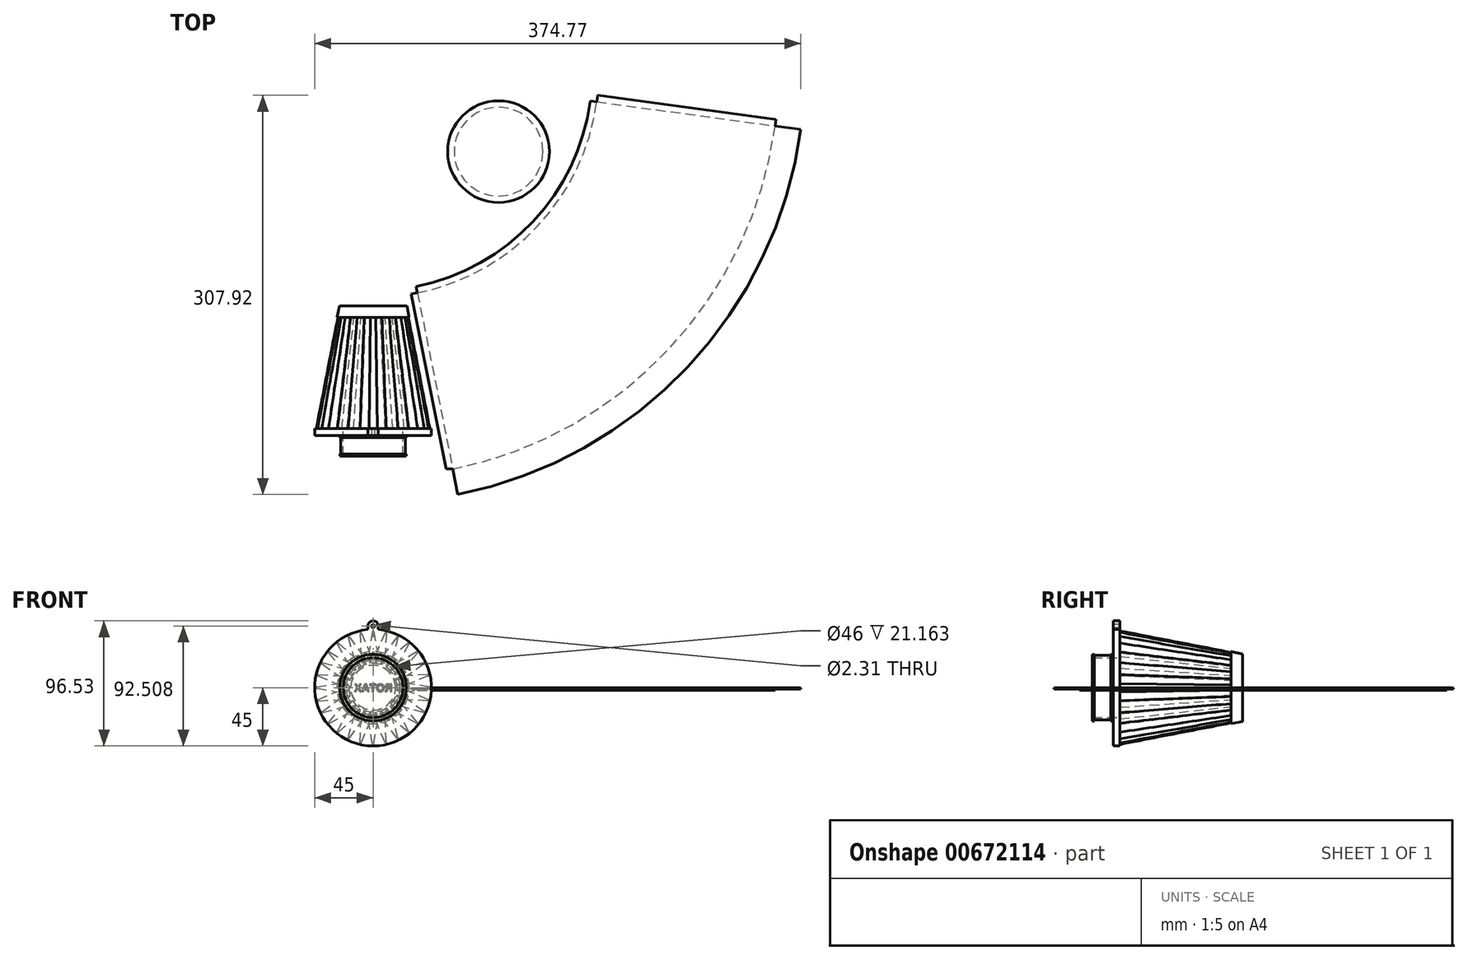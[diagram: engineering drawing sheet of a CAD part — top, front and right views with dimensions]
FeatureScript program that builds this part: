
annotation { "Feature Type Name" : "Feature", "Feature Type Description" : "" }
export const myFeature = defineFeature(function(context is Context, id is Id, definition is map)
    precondition{}
    {
        {
            var Q0;
            Q0=qCreatedBy(makeId("Top.planeOp"),FACE);
            var sketch = newSketch(context, id + "F0", { "sketchPlane" : qUnion([Q0])});
            skLineSegment(sketch, "E0", {"start": v(0, 51.66) * mm, "end": v(0, -26.1) * mm, "construction": true});
            skLineSegment(sketch, "E1.bottom", {"start": v(23, 0) * mm, "end": v(25.69, 0) * mm});
            skLineSegment(sketch, "E1.top", {"start": v(23, -16) * mm, "end": v(25.69, -16) * mm});
            skLineSegment(sketch, "E1.left", {"start": v(23, 5.16) * mm, "end": v(23, -16) * mm});
            skLineSegment(sketch, "E1.right", {"start": v(25.69, 0) * mm, "end": v(25.69, -1.62) * mm});
            skLineSegment(sketch, "E2.bottom", {"start": v(23, 0) * mm, "end": v(45, 0) * mm});
            skLineSegment(sketch, "E2.top", {"start": v(23, 5.16) * mm, "end": v(45, 5.16) * mm});
            skLineSegment(sketch, "E2.left", {"start": v(0, 0) * mm, "end": v(0, 5.16) * mm});
            skLineSegment(sketch, "E2.right", {"start": v(45, 0) * mm, "end": v(45, 5.16) * mm});
            skLineSegment(sketch, "E3.bottom", {"start": v(0, 100) * mm, "end": v(26, 100) * mm});
            skLineSegment(sketch, "E3.top", {"start": v(0, 90.86) * mm, "end": v(27.83, 90.86) * mm});
            skLineSegment(sketch, "E3.left", {"start": v(0, 100) * mm, "end": v(0, 90.86) * mm});
            skLineSegment(sketch, "E3.right", {"start": v(26, 100) * mm, "end": v(27.83, 90.86) * mm});
            skLineSegment(sketch, "E4", {"start": v(27.83, 90.86) * mm, "end": v(45, 5.16) * mm, "construction": true});
            skLineSegment(sketch, "E5.bottom", {"start": v(23, 5.16) * mm, "end": v(0, 5.16) * mm});
            skLineSegment(sketch, "E5.top", {"start": v(23, 0) * mm, "end": v(0, 0) * mm});
            skLineSegment(sketch, "E5.left", {"start": v(23, 5.16) * mm, "end": v(23, 0) * mm});
            skLineSegment(sketch, "E5.right", {"start": v(0, 5.16) * mm, "end": v(0, 0) * mm});
            skLineSegment(sketch, "E6.bottom", {"start": v(25.69, -14.38) * mm, "end": v(24.93, -14.38) * mm});
            skLineSegment(sketch, "E6.top", {"start": v(25.69, -1.62) * mm, "end": v(24.93, -1.62) * mm});
            skLineSegment(sketch, "E6.right", {"start": v(24.93, -14.38) * mm, "end": v(24.93, -1.62) * mm});
            skLineSegment(sketch, "E7.trimOffspring", {"start": v(25.69, -14.38) * mm, "end": v(25.69, -16) * mm});
            skSolve(sketch);
        }
        {
            var Q0;
            Q0=makeQuery(id+"F0.imprint","IMPRINT",FACE,{"disambiguationData":[TD([[makeQuery(id+"F0.imprint","IMPRINT",EDGE,{"derivedFrom":sQuery(id+"F0.wireOp",EDGE,"E3.bottom")}),-1.0]])]});
            var Q1;
            Q1=makeQuery(id+"F0.imprint","IMPRINT",FACE,{"disambiguationData":[TD([[makeQuery(id+"F0.imprint","IMPRINT",EDGE,{"derivedFrom":sQuery(id+"F0.wireOp",EDGE,"E1.top")}),1.0]])]});
            var Q2;
            Q2=makeQuery(id+"F0.imprint","IMPRINT",FACE,{"disambiguationData":[TD([[makeQuery(id+"F0.imprint","IMPRINT",EDGE,{"derivedFrom":sQuery(id+"F0.wireOp",EDGE,"E5.bottom")}),1.0]])]});
            var Q3;
            Q3=makeQuery(id+"F0.imprint","IMPRINT",FACE,{"disambiguationData":[TD([[makeQuery(id+"F0.imprint","IMPRINT",EDGE,{"derivedFrom":sQuery(id+"F0.wireOp",EDGE,"E2.top")}),-1.0]])]});
            var Q4;
            Q4=sQuery(id+"F0.wireOp",EDGE,"E0");
            revolve(context, id + "F1", {"entities" : qUnion([Q0, Q1, Q2, Q3]), "axis" : qUnion([Q4]), "revolveType" : RevolveType.FULL});
        }
        {
            var Q0;
            Q0=makeQuery(id+"F1.opRevolve","SWEPT_FACE",FACE,{"disambiguationData":[OSD([sQuery(id+"F0.wireOp",EDGE,"E2.top")])]});
            var sketch = newSketch(context, id + "F2", { "sketchPlane" : qUnion([Q0])});
            skLineSegment(sketch, "E8", {"start": v(0.5, 43.39) * mm, "end": v(3.18, 28.2) * mm});
            skLineSegment(sketch, "E9", {"start": v(0, 17.46) * mm, "end": v(0, -16.12) * mm, "construction": true});
            skLineSegment(sketch, "E10.MirrorCS", {"start": v(-0.5, 43.39) * mm, "end": v(-3.18, 28.2) * mm});
            skPoint(sketch, "E11.visualSharp", {"position": v(0, 46.17) * mm});
            skArc(sketch, "E11.filletArc", {"start": v(0.5, 43.39) * mm, "mid": v(0, 43.8) * mm, "end": v(-0.5, 43.39) * mm});
            skLineSegment(sketch, "E12.1.0", {"start": v(-10.13, 42.2) * mm, "end": v(-9.37, 26.79) * mm});
            skArc(sketch, "E12.1.1", {"start": v(-9.17, 42.41) * mm, "mid": v(-9.75, 42.7) * mm, "end": v(-10.13, 42.2) * mm});
            skLineSegment(sketch, "E12.1.2", {"start": v(-9.17, 42.41) * mm, "end": v(-3.18, 28.2) * mm});
            skLineSegment(sketch, "E12.2.0", {"start": v(-19.27, 38.88) * mm, "end": v(-15.1, 24.03) * mm});
            skArc(sketch, "E12.2.1", {"start": v(-18.38, 39.3) * mm, "mid": v(-19, 39.46) * mm, "end": v(-19.27, 38.88) * mm});
            skLineSegment(sketch, "E12.2.2", {"start": v(-18.38, 39.3) * mm, "end": v(-9.37, 26.79) * mm});
            skLineSegment(sketch, "E12.3.0", {"start": v(-27.44, 33.62) * mm, "end": v(-20.07, 20.07) * mm});
            skArc(sketch, "E12.3.1", {"start": v(-26.67, 34.23) * mm, "mid": v(-27.31, 34.25) * mm, "end": v(-27.44, 33.62) * mm});
            skLineSegment(sketch, "E12.3.2", {"start": v(-26.67, 34.23) * mm, "end": v(-15.1, 24.03) * mm});
            skLineSegment(sketch, "E12.4.0", {"start": v(-34.23, 26.67) * mm, "end": v(-24.03, 15.1) * mm});
            skArc(sketch, "E12.4.1", {"start": v(-33.62, 27.44) * mm, "mid": v(-34.25, 27.31) * mm, "end": v(-34.23, 26.67) * mm});
            skLineSegment(sketch, "E12.4.2", {"start": v(-33.62, 27.44) * mm, "end": v(-20.07, 20.07) * mm});
            skLineSegment(sketch, "E12.5.0", {"start": v(-39.3, 18.38) * mm, "end": v(-26.79, 9.37) * mm});
            skArc(sketch, "E12.5.1", {"start": v(-38.88, 19.27) * mm, "mid": v(-39.46, 19) * mm, "end": v(-39.3, 18.38) * mm});
            skLineSegment(sketch, "E12.5.2", {"start": v(-38.88, 19.27) * mm, "end": v(-24.03, 15.1) * mm});
            skLineSegment(sketch, "E12.6.0", {"start": v(-42.41, 9.17) * mm, "end": v(-28.2, 3.18) * mm});
            skArc(sketch, "E12.6.1", {"start": v(-42.2, 10.13) * mm, "mid": v(-42.7, 9.75) * mm, "end": v(-42.41, 9.17) * mm});
            skLineSegment(sketch, "E12.6.2", {"start": v(-42.2, 10.13) * mm, "end": v(-26.79, 9.37) * mm});
            skLineSegment(sketch, "E12.7.0", {"start": v(-43.39, -0.5) * mm, "end": v(-28.2, -3.18) * mm});
            skArc(sketch, "E12.7.1", {"start": v(-43.39, 0.5) * mm, "mid": v(-43.8, 0) * mm, "end": v(-43.39, -0.5) * mm});
            skLineSegment(sketch, "E12.7.2", {"start": v(-43.39, 0.5) * mm, "end": v(-28.2, 3.18) * mm});
            skLineSegment(sketch, "E12.8.0", {"start": v(-42.2, -10.13) * mm, "end": v(-26.79, -9.37) * mm});
            skArc(sketch, "E12.8.1", {"start": v(-42.41, -9.17) * mm, "mid": v(-42.7, -9.75) * mm, "end": v(-42.2, -10.13) * mm});
            skLineSegment(sketch, "E12.8.2", {"start": v(-42.41, -9.17) * mm, "end": v(-28.2, -3.18) * mm});
            skLineSegment(sketch, "E12.9.0", {"start": v(-38.88, -19.27) * mm, "end": v(-24.03, -15.1) * mm});
            skArc(sketch, "E12.9.1", {"start": v(-39.3, -18.38) * mm, "mid": v(-39.46, -19) * mm, "end": v(-38.88, -19.27) * mm});
            skLineSegment(sketch, "E12.9.2", {"start": v(-39.3, -18.38) * mm, "end": v(-26.79, -9.37) * mm});
            skLineSegment(sketch, "E12.10.0", {"start": v(-33.62, -27.44) * mm, "end": v(-20.07, -20.07) * mm});
            skArc(sketch, "E12.10.1", {"start": v(-34.23, -26.67) * mm, "mid": v(-34.25, -27.31) * mm, "end": v(-33.62, -27.44) * mm});
            skLineSegment(sketch, "E12.10.2", {"start": v(-34.23, -26.67) * mm, "end": v(-24.03, -15.1) * mm});
            skLineSegment(sketch, "E12.11.0", {"start": v(-26.67, -34.23) * mm, "end": v(-15.1, -24.03) * mm});
            skArc(sketch, "E12.11.1", {"start": v(-27.44, -33.62) * mm, "mid": v(-27.31, -34.25) * mm, "end": v(-26.67, -34.23) * mm});
            skLineSegment(sketch, "E12.11.2", {"start": v(-27.44, -33.62) * mm, "end": v(-20.07, -20.07) * mm});
            skLineSegment(sketch, "E12.12.0", {"start": v(-18.38, -39.3) * mm, "end": v(-9.37, -26.79) * mm});
            skArc(sketch, "E12.12.1", {"start": v(-19.27, -38.88) * mm, "mid": v(-19, -39.46) * mm, "end": v(-18.38, -39.3) * mm});
            skLineSegment(sketch, "E12.12.2", {"start": v(-19.27, -38.88) * mm, "end": v(-15.1, -24.03) * mm});
            skLineSegment(sketch, "E12.13.0", {"start": v(-9.17, -42.41) * mm, "end": v(-3.18, -28.2) * mm});
            skArc(sketch, "E12.13.1", {"start": v(-10.13, -42.2) * mm, "mid": v(-9.75, -42.7) * mm, "end": v(-9.17, -42.41) * mm});
            skLineSegment(sketch, "E12.13.2", {"start": v(-10.13, -42.2) * mm, "end": v(-9.37, -26.79) * mm});
            skLineSegment(sketch, "E12.14.0", {"start": v(0.5, -43.39) * mm, "end": v(3.18, -28.2) * mm});
            skArc(sketch, "E12.14.1", {"start": v(-0.5, -43.39) * mm, "mid": v(0, -43.8) * mm, "end": v(0.5, -43.39) * mm});
            skLineSegment(sketch, "E12.14.2", {"start": v(-0.5, -43.39) * mm, "end": v(-3.18, -28.2) * mm});
            skLineSegment(sketch, "E12.15.0", {"start": v(10.13, -42.2) * mm, "end": v(9.37, -26.79) * mm});
            skArc(sketch, "E12.15.1", {"start": v(9.17, -42.41) * mm, "mid": v(9.75, -42.7) * mm, "end": v(10.13, -42.2) * mm});
            skLineSegment(sketch, "E12.15.2", {"start": v(9.17, -42.41) * mm, "end": v(3.18, -28.2) * mm});
            skLineSegment(sketch, "E12.16.0", {"start": v(19.27, -38.88) * mm, "end": v(15.1, -24.03) * mm});
            skArc(sketch, "E12.16.1", {"start": v(18.38, -39.3) * mm, "mid": v(19, -39.46) * mm, "end": v(19.27, -38.88) * mm});
            skLineSegment(sketch, "E12.16.2", {"start": v(18.38, -39.3) * mm, "end": v(9.37, -26.79) * mm});
            skLineSegment(sketch, "E12.17.0", {"start": v(27.44, -33.62) * mm, "end": v(20.07, -20.07) * mm});
            skArc(sketch, "E12.17.1", {"start": v(26.67, -34.23) * mm, "mid": v(27.31, -34.25) * mm, "end": v(27.44, -33.62) * mm});
            skLineSegment(sketch, "E12.17.2", {"start": v(26.67, -34.23) * mm, "end": v(15.1, -24.03) * mm});
            skLineSegment(sketch, "E12.18.0", {"start": v(34.23, -26.67) * mm, "end": v(24.03, -15.1) * mm});
            skArc(sketch, "E12.18.1", {"start": v(33.62, -27.44) * mm, "mid": v(34.25, -27.31) * mm, "end": v(34.23, -26.67) * mm});
            skLineSegment(sketch, "E12.18.2", {"start": v(33.62, -27.44) * mm, "end": v(20.07, -20.07) * mm});
            skLineSegment(sketch, "E12.19.0", {"start": v(39.3, -18.38) * mm, "end": v(26.79, -9.37) * mm});
            skArc(sketch, "E12.19.1", {"start": v(38.88, -19.27) * mm, "mid": v(39.46, -19) * mm, "end": v(39.3, -18.38) * mm});
            skLineSegment(sketch, "E12.19.2", {"start": v(38.88, -19.27) * mm, "end": v(24.03, -15.1) * mm});
            skLineSegment(sketch, "E12.20.0", {"start": v(42.41, -9.17) * mm, "end": v(28.2, -3.18) * mm});
            skArc(sketch, "E12.20.1", {"start": v(42.2, -10.13) * mm, "mid": v(42.7, -9.75) * mm, "end": v(42.41, -9.17) * mm});
            skLineSegment(sketch, "E12.20.2", {"start": v(42.2, -10.13) * mm, "end": v(26.79, -9.37) * mm});
            skLineSegment(sketch, "E12.21.0", {"start": v(43.39, 0.5) * mm, "end": v(28.2, 3.18) * mm});
            skArc(sketch, "E12.21.1", {"start": v(43.39, -0.5) * mm, "mid": v(43.8, 0) * mm, "end": v(43.39, 0.5) * mm});
            skLineSegment(sketch, "E12.21.2", {"start": v(43.39, -0.5) * mm, "end": v(28.2, -3.18) * mm});
            skLineSegment(sketch, "E12.22.0", {"start": v(42.2, 10.13) * mm, "end": v(26.79, 9.37) * mm});
            skArc(sketch, "E12.22.1", {"start": v(42.41, 9.17) * mm, "mid": v(42.7, 9.75) * mm, "end": v(42.2, 10.13) * mm});
            skLineSegment(sketch, "E12.22.2", {"start": v(42.41, 9.17) * mm, "end": v(28.2, 3.18) * mm});
            skLineSegment(sketch, "E12.23.0", {"start": v(38.88, 19.27) * mm, "end": v(24.03, 15.1) * mm});
            skArc(sketch, "E12.23.1", {"start": v(39.3, 18.38) * mm, "mid": v(39.46, 19) * mm, "end": v(38.88, 19.27) * mm});
            skLineSegment(sketch, "E12.23.2", {"start": v(39.3, 18.38) * mm, "end": v(26.79, 9.37) * mm});
            skPoint(sketch, "E12.center", {"position": v(0, 0) * mm});
            skLineSegment(sketch, "E13.2.24.0", {"start": v(33.62, 27.44) * mm, "end": v(20.07, 20.07) * mm});
            skArc(sketch, "E13.3.24.0", {"start": v(34.23, 26.67) * mm, "mid": v(34.25, 27.31) * mm, "end": v(33.62, 27.44) * mm});
            skLineSegment(sketch, "E13.7.24.0", {"start": v(34.23, 26.67) * mm, "end": v(24.03, 15.1) * mm});
            skLineSegment(sketch, "E13.2.25.0", {"start": v(26.67, 34.23) * mm, "end": v(15.1, 24.03) * mm});
            skArc(sketch, "E13.3.25.0", {"start": v(27.44, 33.62) * mm, "mid": v(27.31, 34.25) * mm, "end": v(26.67, 34.23) * mm});
            skLineSegment(sketch, "E13.7.25.0", {"start": v(27.44, 33.62) * mm, "end": v(20.07, 20.07) * mm});
            skLineSegment(sketch, "E13.2.26.0", {"start": v(18.38, 39.3) * mm, "end": v(9.37, 26.79) * mm});
            skArc(sketch, "E13.3.26.0", {"start": v(19.27, 38.88) * mm, "mid": v(19, 39.46) * mm, "end": v(18.38, 39.3) * mm});
            skLineSegment(sketch, "E13.7.26.0", {"start": v(19.27, 38.88) * mm, "end": v(15.1, 24.03) * mm});
            skLineSegment(sketch, "E13.2.27.0", {"start": v(9.17, 42.41) * mm, "end": v(3.18, 28.2) * mm});
            skArc(sketch, "E13.3.27.0", {"start": v(10.13, 42.2) * mm, "mid": v(9.75, 42.7) * mm, "end": v(9.17, 42.41) * mm});
            skLineSegment(sketch, "E13.7.27.0", {"start": v(10.13, 42.2) * mm, "end": v(9.37, 26.79) * mm});
            skSolve(sketch);
        }
        {
            var Q0;
            Q0=makeQuery(id+"F1.opRevolve","SWEPT_FACE",FACE,{"disambiguationData":[OSD([sQuery(id+"F0.wireOp",EDGE,"E3.top")])]});
            var sketch = newSketch(context, id + "F3", { "sketchPlane" : qUnion([Q0])});
            skLineSegment(sketch, "E14", {"start": v(0, 0) * mm, "end": v(0, 35.69) * mm, "construction": true});
            skLineSegment(sketch, "E15", {"start": v(1, 26.37) * mm, "end": v(1.96, 17.37) * mm});
            skLineSegment(sketch, "E16.MirrorCS", {"start": v(-1, 26.37) * mm, "end": v(-1.96, 17.37) * mm});
            skPoint(sketch, "E17.visualSharp", {"position": v(0, 35.69) * mm});
            skArc(sketch, "E17.filletArc", {"start": v(1, 26.37) * mm, "mid": v(0, 27.27) * mm, "end": v(-1, 26.37) * mm});
            skLineSegment(sketch, "E18.1.0", {"start": v(-6.84, 25.5) * mm, "end": v(-5.77, 16.5) * mm});
            skArc(sketch, "E18.1.1", {"start": v(-4.9, 25.93) * mm, "mid": v(-6.07, 26.58) * mm, "end": v(-6.84, 25.5) * mm});
            skLineSegment(sketch, "E18.1.2", {"start": v(-4.9, 25.93) * mm, "end": v(-1.96, 17.37) * mm});
            skLineSegment(sketch, "E18.2.0", {"start": v(-12.33, 23.33) * mm, "end": v(-9.3, 14.8) * mm});
            skArc(sketch, "E18.2.1", {"start": v(-10.54, 24.2) * mm, "mid": v(-11.83, 24.57) * mm, "end": v(-12.33, 23.33) * mm});
            skLineSegment(sketch, "E18.2.2", {"start": v(-10.54, 24.2) * mm, "end": v(-5.77, 16.5) * mm});
            skLineSegment(sketch, "E18.3.0", {"start": v(-17.21, 20) * mm, "end": v(-12.35, 12.36) * mm});
            skArc(sketch, "E18.3.1", {"start": v(-15.66, 21.24) * mm, "mid": v(-17, 21.32) * mm, "end": v(-17.21, 20) * mm});
            skLineSegment(sketch, "E18.3.2", {"start": v(-15.66, 21.24) * mm, "end": v(-9.3, 14.8) * mm});
            skLineSegment(sketch, "E18.4.0", {"start": v(-21.23, 15.67) * mm, "end": v(-14.79, 9.3) * mm});
            skArc(sketch, "E18.4.1", {"start": v(-20, 17.22) * mm, "mid": v(-21.31, 17) * mm, "end": v(-21.23, 15.67) * mm});
            skLineSegment(sketch, "E18.4.2", {"start": v(-20, 17.22) * mm, "end": v(-12.35, 12.36) * mm});
            skLineSegment(sketch, "E18.5.0", {"start": v(-24.18, 10.55) * mm, "end": v(-16.49, 5.78) * mm});
            skArc(sketch, "E18.5.1", {"start": v(-23.32, 12.34) * mm, "mid": v(-24.56, 11.84) * mm, "end": v(-24.18, 10.55) * mm});
            skLineSegment(sketch, "E18.5.2", {"start": v(-23.32, 12.34) * mm, "end": v(-14.79, 9.3) * mm});
            skLineSegment(sketch, "E18.6.0", {"start": v(-25.92, 4.9) * mm, "end": v(-17.36, 1.96) * mm});
            skArc(sketch, "E18.6.1", {"start": v(-25.48, 6.84) * mm, "mid": v(-26.57, 6.07) * mm, "end": v(-25.92, 4.9) * mm});
            skLineSegment(sketch, "E18.6.2", {"start": v(-25.48, 6.84) * mm, "end": v(-16.49, 5.78) * mm});
            skLineSegment(sketch, "E18.7.0", {"start": v(-26.36, -0.99) * mm, "end": v(-17.36, -1.95) * mm});
            skArc(sketch, "E18.7.1", {"start": v(-26.36, 1) * mm, "mid": v(-27.26, 0) * mm, "end": v(-26.36, -0.99) * mm});
            skLineSegment(sketch, "E18.7.2", {"start": v(-26.36, 1) * mm, "end": v(-17.36, 1.96) * mm});
            skLineSegment(sketch, "E18.8.0", {"start": v(-25.48, -6.83) * mm, "end": v(-16.49, -5.76) * mm});
            skArc(sketch, "E18.8.1", {"start": v(-25.92, -4.89) * mm, "mid": v(-26.57, -6.06) * mm, "end": v(-25.48, -6.83) * mm});
            skLineSegment(sketch, "E18.8.2", {"start": v(-25.92, -4.89) * mm, "end": v(-17.36, -1.95) * mm});
            skLineSegment(sketch, "E18.9.0", {"start": v(-23.32, -12.33) * mm, "end": v(-14.79, -9.28) * mm});
            skArc(sketch, "E18.9.1", {"start": v(-24.18, -10.53) * mm, "mid": v(-24.56, -11.82) * mm, "end": v(-23.32, -12.33) * mm});
            skLineSegment(sketch, "E18.9.2", {"start": v(-24.18, -10.53) * mm, "end": v(-16.49, -5.76) * mm});
            skLineSegment(sketch, "E18.10.0", {"start": v(-20, -17.2) * mm, "end": v(-12.35, -12.34) * mm});
            skArc(sketch, "E18.10.1", {"start": v(-21.23, -15.65) * mm, "mid": v(-21.31, -16.99) * mm, "end": v(-20, -17.2) * mm});
            skLineSegment(sketch, "E18.10.2", {"start": v(-21.23, -15.65) * mm, "end": v(-14.79, -9.28) * mm});
            skLineSegment(sketch, "E18.11.0", {"start": v(-15.66, -21.22) * mm, "end": v(-9.3, -14.78) * mm});
            skArc(sketch, "E18.11.1", {"start": v(-17.21, -19.98) * mm, "mid": v(-17, -21.3) * mm, "end": v(-15.66, -21.22) * mm});
            skLineSegment(sketch, "E18.11.2", {"start": v(-17.21, -19.98) * mm, "end": v(-12.35, -12.34) * mm});
            skLineSegment(sketch, "E18.12.0", {"start": v(-10.54, -24.18) * mm, "end": v(-5.77, -16.48) * mm});
            skArc(sketch, "E18.12.1", {"start": v(-12.33, -23.31) * mm, "mid": v(-11.83, -24.55) * mm, "end": v(-10.54, -24.18) * mm});
            skLineSegment(sketch, "E18.12.2", {"start": v(-12.33, -23.31) * mm, "end": v(-9.3, -14.78) * mm});
            skLineSegment(sketch, "E18.13.0", {"start": v(-4.9, -25.92) * mm, "end": v(-1.96, -17.35) * mm});
            skArc(sketch, "E18.13.1", {"start": v(-6.84, -25.47) * mm, "mid": v(-6.07, -26.57) * mm, "end": v(-4.9, -25.92) * mm});
            skLineSegment(sketch, "E18.13.2", {"start": v(-6.84, -25.47) * mm, "end": v(-5.77, -16.48) * mm});
            skLineSegment(sketch, "E18.14.0", {"start": v(1, -26.36) * mm, "end": v(1.96, -17.35) * mm});
            skArc(sketch, "E18.14.1", {"start": v(-1, -26.36) * mm, "mid": v(0, -27.25) * mm, "end": v(1, -26.36) * mm});
            skLineSegment(sketch, "E18.14.2", {"start": v(-1, -26.36) * mm, "end": v(-1.96, -17.35) * mm});
            skLineSegment(sketch, "E18.15.0", {"start": v(6.84, -25.47) * mm, "end": v(5.77, -16.48) * mm});
            skArc(sketch, "E18.15.1", {"start": v(4.9, -25.92) * mm, "mid": v(6.07, -26.57) * mm, "end": v(6.84, -25.47) * mm});
            skLineSegment(sketch, "E18.15.2", {"start": v(4.9, -25.92) * mm, "end": v(1.96, -17.35) * mm});
            skLineSegment(sketch, "E18.16.0", {"start": v(12.33, -23.31) * mm, "end": v(9.3, -14.78) * mm});
            skArc(sketch, "E18.16.1", {"start": v(10.54, -24.18) * mm, "mid": v(11.83, -24.55) * mm, "end": v(12.33, -23.31) * mm});
            skLineSegment(sketch, "E18.16.2", {"start": v(10.54, -24.18) * mm, "end": v(5.77, -16.48) * mm});
            skLineSegment(sketch, "E18.17.0", {"start": v(17.21, -19.98) * mm, "end": v(12.35, -12.34) * mm});
            skArc(sketch, "E18.17.1", {"start": v(15.66, -21.22) * mm, "mid": v(17, -21.3) * mm, "end": v(17.21, -19.98) * mm});
            skLineSegment(sketch, "E18.17.2", {"start": v(15.66, -21.22) * mm, "end": v(9.3, -14.78) * mm});
            skLineSegment(sketch, "E18.18.0", {"start": v(21.23, -15.65) * mm, "end": v(14.79, -9.28) * mm});
            skArc(sketch, "E18.18.1", {"start": v(20, -17.2) * mm, "mid": v(21.31, -16.99) * mm, "end": v(21.23, -15.65) * mm});
            skLineSegment(sketch, "E18.18.2", {"start": v(20, -17.2) * mm, "end": v(12.35, -12.34) * mm});
            skLineSegment(sketch, "E18.19.0", {"start": v(24.18, -10.53) * mm, "end": v(16.49, -5.76) * mm});
            skArc(sketch, "E18.19.1", {"start": v(23.32, -12.33) * mm, "mid": v(24.56, -11.82) * mm, "end": v(24.18, -10.53) * mm});
            skLineSegment(sketch, "E18.19.2", {"start": v(23.32, -12.33) * mm, "end": v(14.79, -9.28) * mm});
            skLineSegment(sketch, "E18.20.0", {"start": v(25.92, -4.89) * mm, "end": v(17.36, -1.95) * mm});
            skArc(sketch, "E18.20.1", {"start": v(25.48, -6.83) * mm, "mid": v(26.57, -6.06) * mm, "end": v(25.92, -4.89) * mm});
            skLineSegment(sketch, "E18.20.2", {"start": v(25.48, -6.83) * mm, "end": v(16.49, -5.76) * mm});
            skLineSegment(sketch, "E18.21.0", {"start": v(26.36, 1) * mm, "end": v(17.36, 1.96) * mm});
            skArc(sketch, "E18.21.1", {"start": v(26.36, -0.99) * mm, "mid": v(27.26, 0) * mm, "end": v(26.36, 1) * mm});
            skLineSegment(sketch, "E18.21.2", {"start": v(26.36, -0.99) * mm, "end": v(17.36, -1.95) * mm});
            skLineSegment(sketch, "E18.22.0", {"start": v(25.48, 6.84) * mm, "end": v(16.49, 5.78) * mm});
            skArc(sketch, "E18.22.1", {"start": v(25.92, 4.9) * mm, "mid": v(26.57, 6.07) * mm, "end": v(25.48, 6.84) * mm});
            skLineSegment(sketch, "E18.22.2", {"start": v(25.92, 4.9) * mm, "end": v(17.36, 1.96) * mm});
            skLineSegment(sketch, "E18.23.0", {"start": v(23.32, 12.34) * mm, "end": v(14.79, 9.3) * mm});
            skArc(sketch, "E18.23.1", {"start": v(24.18, 10.55) * mm, "mid": v(24.56, 11.84) * mm, "end": v(23.32, 12.34) * mm});
            skLineSegment(sketch, "E18.23.2", {"start": v(24.18, 10.55) * mm, "end": v(16.49, 5.78) * mm});
            skPoint(sketch, "E18.center", {"position": v(0, 0) * mm});
            skLineSegment(sketch, "E19.2.24.0", {"start": v(20, 17.22) * mm, "end": v(12.35, 12.36) * mm});
            skArc(sketch, "E19.3.24.0", {"start": v(21.23, 15.67) * mm, "mid": v(21.31, 17) * mm, "end": v(20, 17.22) * mm});
            skLineSegment(sketch, "E19.7.24.0", {"start": v(21.23, 15.67) * mm, "end": v(14.79, 9.3) * mm});
            skLineSegment(sketch, "E19.2.25.0", {"start": v(15.66, 21.24) * mm, "end": v(9.3, 14.8) * mm});
            skArc(sketch, "E19.3.25.0", {"start": v(17.21, 20) * mm, "mid": v(17, 21.32) * mm, "end": v(15.66, 21.24) * mm});
            skLineSegment(sketch, "E19.7.25.0", {"start": v(17.21, 20) * mm, "end": v(12.35, 12.36) * mm});
            skLineSegment(sketch, "E19.2.26.0", {"start": v(10.54, 24.2) * mm, "end": v(5.77, 16.5) * mm});
            skArc(sketch, "E19.3.26.0", {"start": v(12.33, 23.33) * mm, "mid": v(11.83, 24.57) * mm, "end": v(10.54, 24.2) * mm});
            skLineSegment(sketch, "E19.7.26.0", {"start": v(12.33, 23.33) * mm, "end": v(9.3, 14.8) * mm});
            skLineSegment(sketch, "E19.2.27.0", {"start": v(4.9, 25.93) * mm, "end": v(1.96, 17.37) * mm});
            skArc(sketch, "E19.3.27.0", {"start": v(6.84, 25.5) * mm, "mid": v(6.07, 26.58) * mm, "end": v(4.9, 25.93) * mm});
            skLineSegment(sketch, "E19.7.27.0", {"start": v(6.84, 25.5) * mm, "end": v(5.77, 16.5) * mm});
            skSolve(sketch);
        }
        {
            var Q0;
            Q0=makeQuery(id+"F2.imprint","IMPRINT",FACE,{"disambiguationData":[TD([[makeQuery(id+"F2.imprint","IMPRINT",EDGE,{"derivedFrom":sQuery(id+"F2.wireOp",EDGE,"E8")}),-1.0]])]});
            var Q1;
            {var subQ54=sQuery(id+"F3.wireOp",EDGE,"E17.filletArc");Q1=makeQuery(id+"F3.imprint","IMPRINT",FACE,{"disambiguationData":[TD([[makeQuery(id+"F3.imprint","IMPRINT",EDGE,{"derivedFrom":subQ54}),1.0]])]});}
            loft(context, id + "F4", {"sheetProfilesArray" : [{ "sheetProfileEntities" : qUnion([Q0]) }, { "sheetProfileEntities" : qUnion([Q1]) }]});
        }
        {
            var Q0;
            Q0=makeQuery(id+"F1.opRevolve","SWEPT_FACE",FACE,{"disambiguationData":[OSD([sQuery(id+"F0.wireOp",EDGE,"E2.bottom")])]});
            var sketch = newSketch(context, id + "F5", { "sketchPlane" : qUnion([Q0])});
            skCircle(sketch, "E20", {"center": v(0, 47.5) * mm, "radius": 1.16 * mm});
            skCircle(sketch, "E21", {"center": v(0, 47.5) * mm, "radius": 4.02 * mm});
            skLineSegment(sketch, "E22", {"start": v(4.02, 47.5) * mm, "end": v(4.02, 44.82) * mm});
            skLineSegment(sketch, "E23.MirrorCS", {"start": v(-4.02, 47.5) * mm, "end": v(-4.02, 44.82) * mm});
            skSolve(sketch);
        }
        {
            var Q0;
            Q0=makeQuery(id+"F5.imprint","IMPRINT",FACE,{"disambiguationData":[TD([[makeQuery(id+"F5.imprint","IMPRINT",EDGE,{"derivedFrom":sQuery(id+"F5.wireOp",EDGE,"E20")}),-1.0]])]});
            var Q1;
            {var subQ0=sQuery(id+"F5.wireOp",EDGE,"E23.MirrorCS");Q1=makeQuery(id+"F5.imprint","IMPRINT",FACE,{"disambiguationData":[TD([[makeQuery(id+"F5.imprint","IMPRINT",EDGE,{"derivedFrom":subQ0}),1.0]])]});}
            var Q2;
            {var subQ0=sQuery(id+"F5.wireOp",EDGE,"E22");Q2=makeQuery(id+"F5.imprint","IMPRINT",FACE,{"disambiguationData":[TD([[makeQuery(id+"F5.imprint","IMPRINT",EDGE,{"derivedFrom":subQ0}),-1.0]])]});}
            var Q3;
            Q3=makeQuery(id+"F1.opRevolve","SWEPT_FACE",FACE,{"disambiguationData":[OSD([sQuery(id+"F0.wireOp",EDGE,"E2.top"),sQuery(id+"F0.wireOp",EDGE,"E5.bottom")])]});
            extrude(context, id + "F6", {"entities" : qUnion([Q0, Q1, Q2]), "operationType" : NewBodyOperationType.ADD, "endBound" : BoundingType.UP_TO_SURFACE, "oppositeDirection" : true, "depth" : 25 * mm, "endBoundEntityFace" : qUnion([Q3]), "offsetDistance" : 25 * mm});
        }
        {
            var Q0;
            Q0=makeQuery(id+"F1.opRevolve","SWEPT_FACE",FACE,{"disambiguationData":[OSD([sQuery(id+"F0.wireOp",EDGE,"E3.bottom")])]});
            var sketch = newSketch(context, id + "F7", { "sketchPlane" : qUnion([Q0])});
            skCircle(sketch, "E24", {"center": v(0, 0) * mm, "radius": 20.9 * mm});
            skCircle(sketch, "E25", {"center": v(0, 0) * mm, "radius": 18.7 * mm});
            skCircle(sketch, "E26", {"center": v(0, 0) * mm, "radius": 17.27 * mm});
            skText(sketch, "E27", { "text": "ROTAX", "fontName": "Arimo-Bold.ttf"});
            const initialGuessF7  = {"E27": [-0.01496, -0.00302, 1, 0, 0.00605]};
            skSetInitialGuess(sketch, initialGuessF7);
            skSolve(sketch);
        }
        {
            var Q0;
            Q0=makeQuery(id+"F7.imprint","IMPRINT",FACE,{"disambiguationData":[TD([[makeQuery(id+"F7.imprint","IMPRINT",EDGE,{"derivedFrom":sQuery(id+"F7.wireOp",EDGE,"E24")}),1.0]])]});
            var Q1;
            Q1=makeQuery(id+"F7.imprint","IMPRINT",FACE,{"disambiguationData":[TD([[makeQuery(id+"F7.imprint","IMPRINT",EDGE,{"derivedFrom":sQuery(id+"F7.wireOp",EDGE,"E26")}),1.0]])]});
            var Q2;
            Q2=makeQuery(id+"F7.imprint","IMPRINT",FACE,{"disambiguationData":[TD([[makeQuery(id+"F7.imprint","IMPRINT",EDGE,{"derivedFrom":sQuery(id+"F7.wireOp",EDGE,"E27.sketch_text.stroke-12")}),1.0]])]});
            var Q3;
            Q3=makeQuery(id+"F7.imprint","IMPRINT",FACE,{"disambiguationData":[TD([[makeQuery(id+"F7.imprint","IMPRINT",EDGE,{"derivedFrom":sQuery(id+"F7.wireOp",EDGE,"E27.sketch_text.stroke-27")}),1.0]])]});
            var Q4;
            Q4=makeQuery(id+"F7.imprint","IMPRINT",FACE,{"disambiguationData":[TD([[makeQuery(id+"F7.imprint","IMPRINT",EDGE,{"derivedFrom":sQuery(id+"F7.wireOp",EDGE,"E27.sketch_text.stroke-51")}),1.0]])]});
            extrude(context, id + "F8", {"entities" : qUnion([Q0, Q1, Q2, Q3, Q4]), "operationType" : NewBodyOperationType.REMOVE, "oppositeDirection" : true, "depth" : .5 * mm, "offsetDistance" : 25 * mm, "hasDraft" : true, "draftAngle" : 5 * degree, "draftPullDirection" : true});
        }
        {
            var Q0;
            Q0=makeQuery(id+"F1.opRevolve","SWEPT_FACE",FACE,{"disambiguationData":[OSD([sQuery(id+"F0.wireOp",EDGE,"E5.top")])]});
            var Q1;
            {var subQ0=sQuery(id+"F0.wireOp",EDGE,"E5.bottom");var subQ1=sQuery(id+"F0.wireOp",EDGE,"E2.top");Q1=makeQuery(id+"F6.boolean.opBoolean","MERGE",FACE,{"derivedFrom":[makeQuery(id+"F1.opRevolve","SWEPT_FACE",FACE,{"disambiguationData":[OSD([subQ1,subQ0])]}),makeQuery(id+"F6.opExtrude","CAP_FACE",FACE,{"disambiguationData":[OSD([subQ1,subQ0])],"isStart":false})]});}
            extrude(context, id + "F9", {"entities" : qUnion([Q0]), "operationType" : NewBodyOperationType.REMOVE, "endBound" : BoundingType.UP_TO_SURFACE, "oppositeDirection" : true, "depth" : 25 * mm, "endBoundEntityFace" : qUnion([Q1]), "offsetDistance" : 25 * mm});
        }
        {
            var Q0;
            Q0=qCreatedBy(makeId("Top.planeOp"),FACE);
            var sketch = newSketch(context, id + "F10", { "sketchPlane" : qUnion([Q0])});
            skLineSegment(sketch, "E28.0", {"start": v(0, 110) * mm, "end": v(34.2, 110) * mm});
            skLineSegment(sketch, "E29.0", {"start": v(34.2, 110) * mm, "end": v(61.44, -26) * mm});
            skLineSegment(sketch, "E30.0", {"start": v(-25.69, -26) * mm, "end": v(61.44, -26) * mm});
            skLineSegment(sketch, "E31", {"start": v(0, 110) * mm, "end": v(0, -26) * mm});
            skLineSegment(sketch, "E32", {"start": v(0, 110) * mm, "end": v(0, 280.68) * mm, "construction": true});
            skLineSegment(sketch, "E33", {"start": v(0, 280.68) * mm, "end": v(34.2, 110) * mm, "construction": true});
            skArc(sketch, "E34", {"start": v(34.2, 110) * mm, "mid": v(126.91, 161.54) * mm, "end": v(172.5, 257.33) * mm});
            skArc(sketch, "E35", {"start": v(61.44, -26) * mm, "mid": v(228.04, 66.61) * mm, "end": v(309.95, 238.72) * mm});
            skLineSegment(sketch, "E36", {"start": v(0, 280.68) * mm, "end": v(172.5, 257.33) * mm, "construction": true});
            skLineSegment(sketch, "E37", {"start": v(172.5, 257.33) * mm, "end": v(309.95, 238.72) * mm});
            skCircle(sketch, "E38", {"center": v(96.73, 218.87) * mm, "radius": 34.2 * mm});
            skLineSegment(sketch, "E39", {"start": v(96.73, 218.87) * mm, "end": v(63.9, 209.33) * mm, "construction": true});
            skArc(sketch, "E40.0", {"start": v(65.2, -45.64) * mm, "mid": v(242.57, 52.86) * mm, "end": v(329.77, 236.04) * mm});
            skLineSegment(sketch, "E41", {"start": v(309.95, 238.72) * mm, "end": v(329.77, 236.04) * mm, "construction": true});
            skLineSegment(sketch, "E42", {"start": v(61.44, -26) * mm, "end": v(65.2, -45.64) * mm, "construction": true});
            skCircle(sketch, "E43.0", {"center": v(96.73, 218.87) * mm, "radius": 39.2 * mm});
            skArc(sketch, "E44.0", {"start": v(33.25, 114.91) * mm, "mid": v(123.28, 164.98) * mm, "end": v(167.55, 258) * mm});
            skLineSegment(sketch, "E45", {"start": v(33.25, 114.91) * mm, "end": v(34.2, 110) * mm, "construction": true});
            skLineSegment(sketch, "E46", {"start": v(167.55, 258) * mm, "end": v(172.5, 257.33) * mm, "construction": true});
            skLineSegment(sketch, "E47.0", {"start": v(173.21, 262.28) * mm, "end": v(310.66, 243.67) * mm});
            skLineSegment(sketch, "E48", {"start": v(172.5, 257.33) * mm, "end": v(173.21, 262.28) * mm, "construction": true});
            skLineSegment(sketch, "E49", {"start": v(310.66, 243.67) * mm, "end": v(309.95, 238.72) * mm, "construction": true});
            skLineSegment(sketch, "E50.0", {"start": v(29.28, 109.06) * mm, "end": v(56.53, -26.94) * mm});
            skLineSegment(sketch, "E51", {"start": v(29.28, 109.06) * mm, "end": v(34.2, 110) * mm, "construction": true});
            skLineSegment(sketch, "E52", {"start": v(56.53, -26.94) * mm, "end": v(61.44, -26) * mm, "construction": true});
            skLineSegment(sketch, "E53", {"start": v(0, 280.68) * mm, "end": v(185.7, 106.36) * mm});
            skLineSegment(sketch, "E54", {"start": v(185.7, 106.36) * mm, "end": v(242.62, 52.92) * mm});
            skLineSegment(sketch, "E55", {"start": v(173.21, 262.28) * mm, "end": v(172.5, 257.33) * mm});
            skLineSegment(sketch, "E56", {"start": v(310.66, 243.67) * mm, "end": v(309.95, 238.72) * mm});
            skLineSegment(sketch, "E57", {"start": v(309.95, 238.72) * mm, "end": v(329.77, 236.04) * mm});
            skLineSegment(sketch, "E58", {"start": v(65.2, -45.64) * mm, "end": v(61.44, -26) * mm});
            skLineSegment(sketch, "E59", {"start": v(56.53, -26.94) * mm, "end": v(61.44, -26) * mm});
            skLineSegment(sketch, "E60", {"start": v(29.28, 109.06) * mm, "end": v(34.2, 110) * mm});
            skLineSegment(sketch, "E61", {"start": v(33.25, 114.91) * mm, "end": v(34.2, 110) * mm});
            skLineSegment(sketch, "E62", {"start": v(167.55, 258) * mm, "end": v(172.5, 257.33) * mm});
            skPoint(sketch, "E63.orphan", {"position": v(228.04, 66.61) * mm});
            skSolve(sketch);
        }
        {
            var Q0;
            {var subQ0=sQuery(id+"F10.wireOp",EDGE,"E53");var subQ1=sQuery(id+"F10.wireOp",EDGE,"E38");var subQ2=makeQuery(id+"F10.imprint","INTERSECT",VERTEX,{"disambiguationData":[OD(0.0)],"derivedFrom":[subQ1,subQ0]});Q0=makeQuery(id+"F10.imprint","IMPRINT",FACE,{"disambiguationData":[TD([[makeQuery(id+"F10.imprint","IMPRINT",EDGE,{"disambiguationData":[TD([[subQ2,1.0]])],"derivedFrom":subQ1}),1.0]])]});}
            var Q1;
            {var subQ4=sQuery(id+"F10.wireOp",EDGE,"E37");Q1=makeQuery(id+"F10.imprint","IMPRINT",FACE,{"disambiguationData":[TD([[makeQuery(id+"F10.imprint","IMPRINT",EDGE,{"derivedFrom":subQ4}),-1.0]])]});}
            var Q2;
            {var subQ0=sQuery(id+"F10.wireOp",EDGE,"E53");var subQ1=sQuery(id+"F10.wireOp",EDGE,"E38");var subQ2=makeQuery(id+"F10.imprint","INTERSECT",VERTEX,{"disambiguationData":[OD(0.0)],"derivedFrom":[subQ1,subQ0]});Q2=makeQuery(id+"F10.imprint","IMPRINT",FACE,{"disambiguationData":[TD([[makeQuery(id+"F10.imprint","IMPRINT",EDGE,{"disambiguationData":[TD([[subQ2,-1.0]])],"derivedFrom":subQ1}),1.0]])]});}
            var Q3;
            {var subQ5=sQuery(id+"F10.wireOp",EDGE,"E29.0");Q3=makeQuery(id+"F10.imprint","IMPRINT",FACE,{"disambiguationData":[TD([[makeQuery(id+"F10.imprint","IMPRINT",EDGE,{"derivedFrom":subQ5}),1.0]])]});}
            extrude(context, id + "F11", {"entities" : qUnion([Q0, Q1, Q2, Q3]), "oppositeDirection" : true, "depth" : 2 * mm, "offsetDistance" : 25 * mm});
        }
        {
            var Q0;
            {var subQ0=sQuery(id+"F10.wireOp",EDGE,"E29.0");Q0=makeQuery(id+"F10.imprint","IMPRINT",FACE,{"disambiguationData":[TD([[makeQuery(id+"F10.imprint","IMPRINT",EDGE,{"derivedFrom":subQ0}),-1.0]])]});}
            var Q1;
            Q1=makeQuery(id+"F10.imprint","IMPRINT",FACE,{"disambiguationData":[TD([[makeQuery(id+"F10.imprint","IMPRINT",EDGE,{"derivedFrom":sQuery(id+"F10.wireOp",EDGE,"E40.0")}),1.0]])]});
            var Q2;
            {var subQ0=sQuery(id+"F10.wireOp",EDGE,"E61");Q2=makeQuery(id+"F10.imprint","IMPRINT",FACE,{"disambiguationData":[TD([[makeQuery(id+"F10.imprint","IMPRINT",EDGE,{"derivedFrom":subQ0}),1.0]])]});}
            var Q3;
            {var subQ0=sQuery(id+"F10.wireOp",EDGE,"E62");Q3=makeQuery(id+"F10.imprint","IMPRINT",FACE,{"disambiguationData":[TD([[makeQuery(id+"F10.imprint","IMPRINT",EDGE,{"derivedFrom":subQ0}),-1.0]])]});}
            var Q4;
            Q4=makeQuery(id+"F10.imprint","IMPRINT",FACE,{"disambiguationData":[TD([[makeQuery(id+"F10.imprint","IMPRINT",EDGE,{"derivedFrom":sQuery(id+"F10.wireOp",EDGE,"E37")}),1.0]])]});
            var Q5;
            {var subQ0=sQuery(id+"F10.wireOp",EDGE,"E53");var subQ1=sQuery(id+"F10.wireOp",EDGE,"E38");var subQ2=makeQuery(id+"F10.imprint","INTERSECT",VERTEX,{"disambiguationData":[OD(0.0)],"derivedFrom":[subQ1,subQ0]});Q5=makeQuery(id+"F10.imprint","IMPRINT",FACE,{"disambiguationData":[TD([[makeQuery(id+"F10.imprint","IMPRINT",EDGE,{"disambiguationData":[TD([[subQ2,1.0]])],"derivedFrom":subQ1}),-1.0]])]});}
            var Q6;
            {var subQ0=sQuery(id+"F10.wireOp",EDGE,"E53");var subQ1=sQuery(id+"F10.wireOp",EDGE,"E38");var subQ2=makeQuery(id+"F10.imprint","INTERSECT",VERTEX,{"disambiguationData":[OD(0.0)],"derivedFrom":[subQ1,subQ0]});Q6=makeQuery(id+"F10.imprint","IMPRINT",FACE,{"disambiguationData":[TD([[makeQuery(id+"F10.imprint","IMPRINT",EDGE,{"disambiguationData":[TD([[subQ2,-1.0]])],"derivedFrom":subQ1}),-1.0]])]});}
            extrude(context, id + "F12", {"entities" : qUnion([Q0, Q1, Q2, Q3, Q4, Q5, Q6]), "operationType" : NewBodyOperationType.ADD, "oppositeDirection" : true, "depth" : 1 * mm, "offsetDistance" : 25 * mm});
        }
    });
